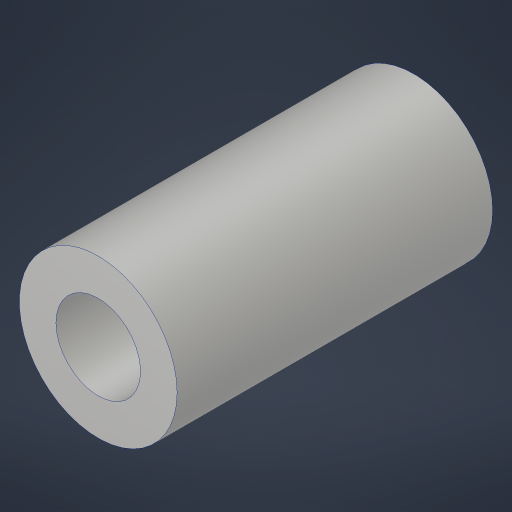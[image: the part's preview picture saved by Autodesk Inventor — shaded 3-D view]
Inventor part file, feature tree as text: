
AUTODESK INVENTOR PART (.ipt)
format: ipt  version: 2023.4 (Build 274418000, 418)  size: 171,520 bytes
history: native  units: in
note: dims shown in document units (in); Inventor stores cm internally (conversion verified against a paired STEP export)
features: extrude x1, hole x1
ambient origin geometry x8: Origin, YZ Plane, XZ Plane, XY Plane, X Axis, Y Axis, Z Axis, Center Point
bodies: Solid1 (feature_tree)
feature tree (2):
  extrude  "Extrusion1"  Depth=0.75in
  hole  "Hole1"  [1 undecoded]
note: 1 required parameter value undecoded (feature->parameter linkage not recoverable at this tier; creation-order binding heuristic only, values carry confidence <= 0.55)
